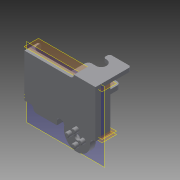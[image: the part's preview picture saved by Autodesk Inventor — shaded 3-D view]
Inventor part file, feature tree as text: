
AUTODESK INVENTOR PART (.ipt)
format: ipt  version: 2014 (Build 180170000, 170)  size: 445,440 bytes
history: native  units: mm
features: extrude x19, sketch x18, fillet x12, other x5
ambient origin geometry x8: Origin, YZ Plane, XZ Plane, XY Plane, X Axis, Y Axis, Z Axis, Center Point
bodies: Body1 (feature_tree)
feature tree (54):
  other  "ソリッド1"
  extrude  "押し出し2"  Depth=14.0mm
  other  "作業平面4"
  extrude  "押し出し3"  Depth=1.0mm TaperAngle=0.0deg
  fillet  "フィレット3"  Radius=3.8mm
  extrude  "押し出し1"  Depth=8.8mm
  fillet  "フィレット4"  Radius=35.8mm
  other  "作業平面5"
  extrude  "押し出し4"  Depth=22.0mm
  other  "作業平面7"
  extrude  "押し出し5"  Depth=1.0mm
  extrude  "押し出し6"  Depth=1.0mm
  fillet  "フィレット5"  Radius=22.0mm
  fillet  "フィレット6"  Radius=22.0mm
  fillet  "フィレット7"  Radius=6.0mm
  fillet  "フィレット8"  Radius=1.0mm
  extrude  "押し出し7"  Depth=22.0mm
  other  "作業平面8"
  extrude  "押し出し8"  Depth=35.8mm
  extrude  "押し出し9"  Depth=8.8mm
  extrude  "押し出し10"  Depth=3.8mm
  extrude  "押し出し11"  Depth=1.0mm TaperAngle=0.0deg
  fillet  "フィレット13"  Radius=5.1mm
  fillet  "フィレット9"  Radius=3.1mm
  extrude  "押し出し12"  Depth=3.8mm
  fillet  "フィレット11"  Radius=5.6mm
  fillet  "フィレット15"  Radius=6.2mm
  extrude  "押し出し13"  Depth=2.1mm
  fillet  "フィレット16"  Radius=2.1mm
  extrude  "押し出し14"  Depth=3.6mm
  extrude  "押し出し15"  Depth=24.9mm
  extrude  "押し出し16"  Depth=5.5mm
  extrude  "押し出し17"  Depth=8.0mm
  extrude  "押し出し18"  TaperAngle=0.0deg  [1 undecoded]
  extrude  "押し出し19"  TaperAngle=0.0deg  [1 undecoded]
  fillet  "フィレット17"  Radius=5.3mm
  sketch  "スケッチ1"
  sketch  "スケッチ2"
  sketch  "スケッチ3"
  sketch  "スケッチ4"
  sketch  "スケッチ7"
  sketch  "スケッチ8"
  sketch  "スケッチ9"
  sketch  "スケッチ10"
  sketch  "スケッチ11"
  sketch  "スケッチ12"
  sketch  "スケッチ13"
  sketch  "スケッチ14"
  sketch  "スケッチ16"
  sketch  "スケッチ17"
  sketch  "スケッチ18"
  sketch  "スケッチ19"
  sketch  "スケッチ21"
  sketch  "スケッチ22"
note: 2 required parameter values undecoded (feature->parameter linkage not recoverable at this tier; creation-order binding heuristic only, values carry confidence <= 0.55)
